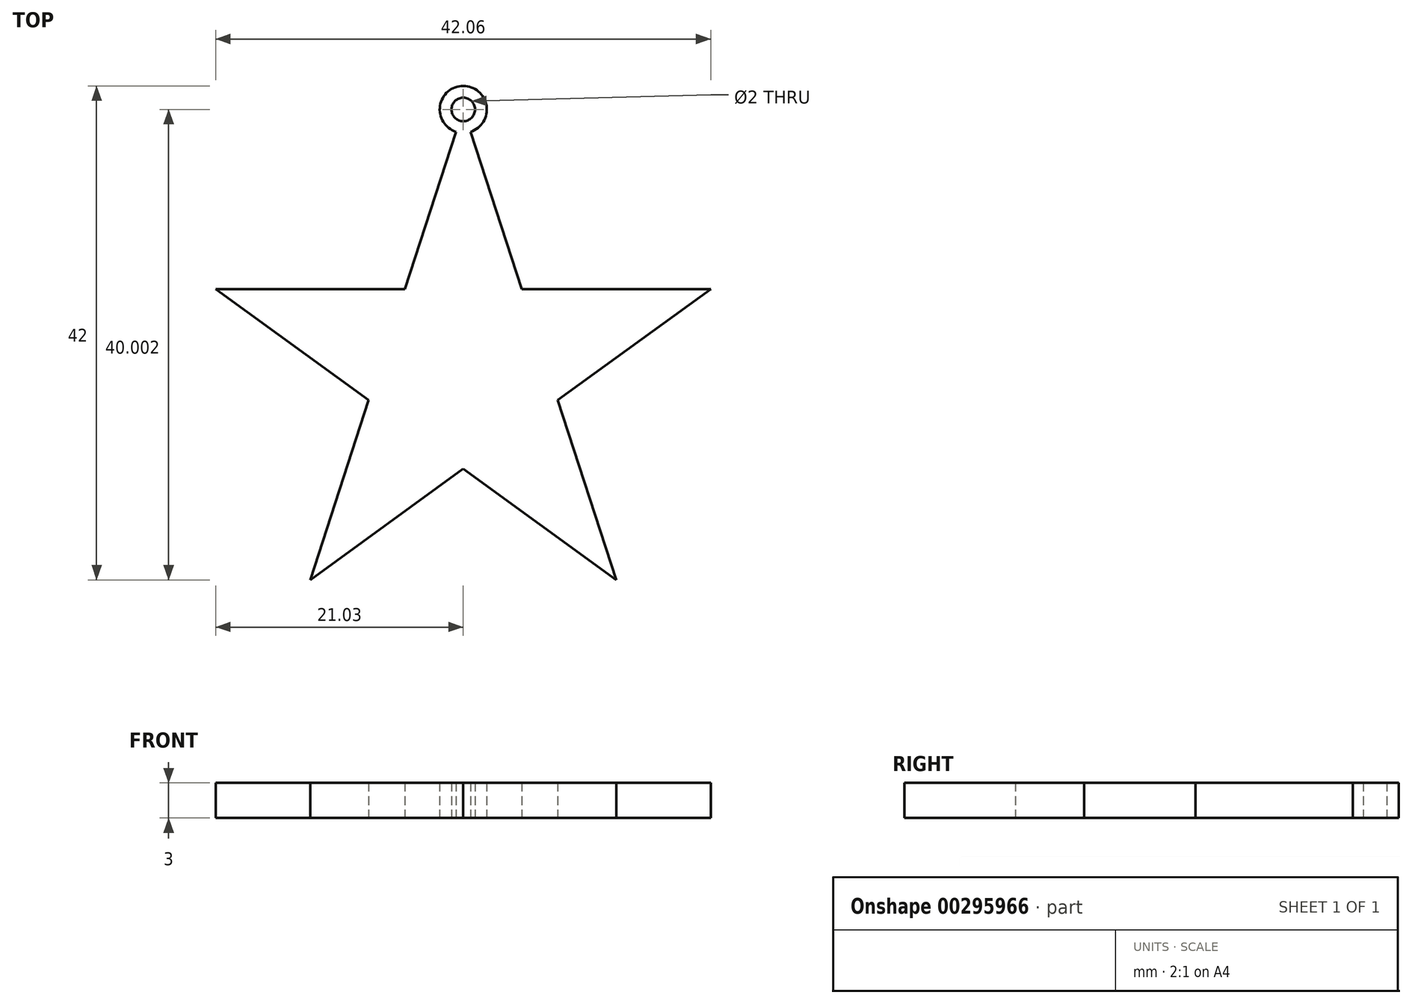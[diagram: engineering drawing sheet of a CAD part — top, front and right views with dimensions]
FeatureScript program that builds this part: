
annotation { "Feature Type Name" : "Feature", "Feature Type Description" : "" }
export const myFeature = defineFeature(function(context is Context, id is Id, definition is map)
    precondition{}
    {
        {
            var Q0;
            Q0=qCreatedBy(makeId("Top.planeOp"),FACE);
            var sketch = newSketch(context, id + "F0", { "sketchPlane" : qUnion([Q0])});
            skCircle(sketch, "E0.cCircle", {"center": v(0, 0) * mm, "radius": 17.89 * mm, "construction": true});
            skLineSegment(sketch, "E0.0", {"start": v(0, 22.11) * mm, "end": v(21.03, 6.83) * mm});
            skLineSegment(sketch, "E0.1", {"start": v(21.03, 6.83) * mm, "end": v(13, -17.89) * mm});
            skLineSegment(sketch, "E0.2", {"start": v(13, -17.89) * mm, "end": v(-13, -17.89) * mm});
            skLineSegment(sketch, "E0.3", {"start": v(-13, -17.89) * mm, "end": v(-21.03, 6.83) * mm});
            skLineSegment(sketch, "E0.4", {"start": v(-21.03, 6.83) * mm, "end": v(0, 22.11) * mm});
            skPoint(sketch, "E0.0.midPoint", {"position": v(10.51, 14.47) * mm});
            skPoint(sketch, "E1.orphan", {"position": v(-10.51, 14.47) * mm});
            skPoint(sketch, "E2.trimOffspring.end.orphan", {"position": v(-17.01, -5.53) * mm});
            skPoint(sketch, "E3.trimOffspring.end.orphan", {"position": v(17.01, -5.53) * mm});
            skPoint(sketch, "E4.orphan", {"position": v(0, -17.89) * mm});
            skLineSegment(sketch, "E5", {"start": v(0, 22.11) * mm, "end": v(-4.96, 6.83) * mm});
            skLineSegment(sketch, "E6", {"start": v(-21.03, 6.83) * mm, "end": v(-4.96, 6.83) * mm});
            skLineSegment(sketch, "E7", {"start": v(21.03, 6.83) * mm, "end": v(8.03, -2.6) * mm});
            skLineSegment(sketch, "E8", {"start": v(13, -17.89) * mm, "end": v(0, -8.45) * mm});
            skLineSegment(sketch, "E9", {"start": v(13, -17.89) * mm, "end": v(8.03, -2.6) * mm});
            skLineSegment(sketch, "E10.trimOffspring", {"start": v(4.96, 6.83) * mm, "end": v(21.03, 6.83) * mm});
            skLineSegment(sketch, "E11.trimOffspring", {"start": v(4.96, 6.83) * mm, "end": v(0, 22.11) * mm});
            skLineSegment(sketch, "E12.trimOffspring", {"start": v(0, -8.45) * mm, "end": v(-13, -17.89) * mm});
            skLineSegment(sketch, "E13.trimOffspring", {"start": v(-8.03, -2.6) * mm, "end": v(-21.03, 6.83) * mm});
            skLineSegment(sketch, "E14.trimOffspring", {"start": v(-8.03, -2.6) * mm, "end": v(-13, -17.89) * mm});
            skCircle(sketch, "E15", {"center": v(0, 22.11) * mm, "radius": 2 * mm});
            skCircle(sketch, "E16", {"center": v(0, 22.11) * mm, "radius": 1 * mm});
            skSolve(sketch);
        }
        {
            var Q0;
            Q0=makeQuery(id+"F0.imprint","IMPRINT",FACE,{"disambiguationData":[TD([[makeQuery(id+"F0.imprint","IMPRINT",EDGE,{"derivedFrom":sQuery(id+"F0.wireOp",EDGE,"XSsLThOJ-ZaQI-v7Vn-JERq-CprFEK3kPXpU")}),1.0]])]});
            var Q1;
            {var subQ4=sQuery(id+"F0.wireOp",EDGE,"E6");Q1=makeQuery(id+"F0.imprint","IMPRINT",FACE,{"disambiguationData":[TD([[makeQuery(id+"F0.imprint","IMPRINT",EDGE,{"derivedFrom":subQ4}),-1.0]])]});}
            var Q2;
            {var subQ0=sQuery(id+"F0.wireOp",EDGE,"E16");var subQ1=sQuery(id+"F0.wireOp",EDGE,"E5");var subQ2=makeQuery(id+"F0.imprint","INTERSECT",VERTEX,{"derivedFrom":[subQ1,subQ0]});Q2=makeQuery(id+"F0.imprint","IMPRINT",FACE,{"disambiguationData":[TD([[makeQuery(id+"F0.imprint","IMPRINT",EDGE,{"disambiguationData":[TD([[subQ2,-1.0]])],"derivedFrom":subQ1}),1.0]])]});}
            var Q3;
            {var subQ0=sQuery(id+"F0.wireOp",EDGE,"E15");var subQ1=sQuery(id+"F0.wireOp",EDGE,"E0.0");var subQ2=makeQuery(id+"F0.imprint","INTERSECT",VERTEX,{"derivedFrom":[subQ1,subQ0]});Q3=makeQuery(id+"F0.imprint","IMPRINT",FACE,{"disambiguationData":[TD([[makeQuery(id+"F0.imprint","IMPRINT",EDGE,{"disambiguationData":[TD([[subQ2,1.0]])],"derivedFrom":subQ1}),-1.0]])]});}
            var Q4;
            {var subQ0=sQuery(id+"F0.wireOp",EDGE,"E15");var subQ1=sQuery(id+"F0.wireOp",EDGE,"E0.0");var subQ2=makeQuery(id+"F0.imprint","INTERSECT",VERTEX,{"derivedFrom":[subQ1,subQ0]});Q4=makeQuery(id+"F0.imprint","IMPRINT",FACE,{"disambiguationData":[TD([[makeQuery(id+"F0.imprint","IMPRINT",EDGE,{"disambiguationData":[TD([[subQ2,1.0]])],"derivedFrom":subQ1}),1.0]])]});}
            var Q5;
            {var subQ0=sQuery(id+"F0.wireOp",EDGE,"E15");var subQ1=sQuery(id+"F0.wireOp",EDGE,"E0.4");var subQ2=makeQuery(id+"F0.imprint","INTERSECT",VERTEX,{"derivedFrom":[subQ1,subQ0]});Q5=makeQuery(id+"F0.imprint","IMPRINT",FACE,{"disambiguationData":[TD([[makeQuery(id+"F0.imprint","IMPRINT",EDGE,{"disambiguationData":[TD([[subQ2,-1.0]])],"derivedFrom":subQ1}),-1.0]])]});}
            extrude(context, id + "F1", {"entities" : qUnion([Q0, Q1, Q2, Q3, Q4, Q5]), "depth" : 3 * mm});
        }
    });
